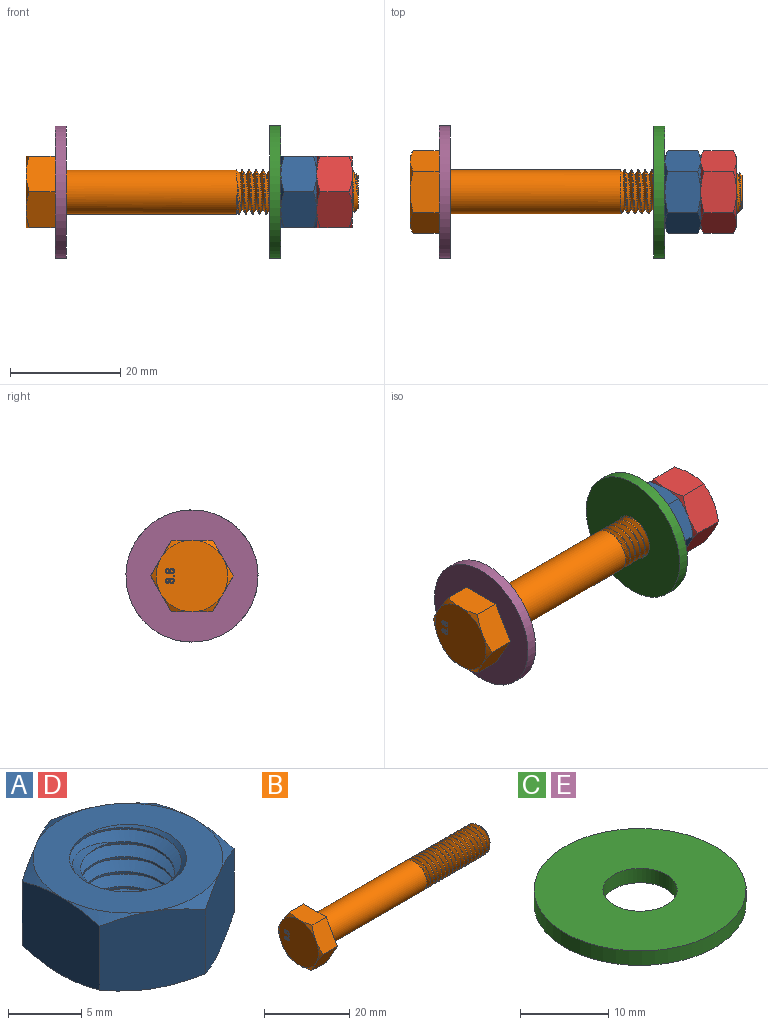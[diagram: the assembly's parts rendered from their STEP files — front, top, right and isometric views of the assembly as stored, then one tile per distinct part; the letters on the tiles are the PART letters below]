
ASSEMBLY  parts=5 mates=4
PART A: 27 faces, bbox 15.6x15.6x9.2 mm
  f0: cylinder r=4mm len=8mm, axis (0,0,-1), area 20.5mm2, adj f10,f11,f12,f13,f14
  f1: cylinder r=3.19mm len=6.38mm, axis (0,0,1), area 12.2mm2, adj f2,f3,f13,f14
  f2: cone r=4mm half-angle=45deg, axis (0,0,-1), area 13.3mm2, adj f1,f11,f13,f14
  f3: cone r=4mm half-angle=45deg, axis (0,0,1), area 13.2mm2, adj f1,f10,f12,f13,f14
  f4: plane 7.12x7.12mm, normal (-0.5,0.87,0), area 45.8mm2, adj f5,f9,f18,f19,f22,f23
  f5: plane 8.12x7.12mm, normal (-1,0,0), area 45.8mm2, adj f4,f6,f17,f18,f23,f24
  f6: plane 7.12x7.12mm, normal (-0.5,-0.87,0), area 45.8mm2, adj f5,f7,f16,f17,f24,f25
  f7: plane 7.12x7.12mm, normal (0.5,-0.87,0), area 45.8mm2, adj f6,f8,f15,f16,f25,f26
  f8: plane 8.12x7.12mm, normal (1,0,0), area 45.8mm2, adj f7,f9,f15,f20,f21,f26
  f9: plane 7.12x7.12mm, normal (0.5,0.87,0), area 45.8mm2, adj f4,f8,f19,f20,f21,f22
  f10: plane 13x13mm, normal (0,0,1), area 82.5mm2, adj f0,f3,f15,f16,f17,f18,f19,f20
  f11: plane 13x13mm, normal (0,0,-1), area 82.5mm2, adj f0,f2,f21,f22,f23,f24,f25,f26
  f12: plane 0.09x0.06mm, normal (-1,0,0), area 0mm2, adj f0,f3,f13
  f13: bspline ~8x7.98mm, area 96.9mm2, adj f0,f1,f2,f3,f12
  f14: bspline ~8.22x8mm, area 107.5mm2, adj f0,f1,f2,f3
  f15: cone r=6.5mm half-angle=60deg, axis (0,0,-1), area 4.2mm2, adj f7,f8,f10
  f16: cone r=6.5mm half-angle=60deg, axis (0,0,-1), area 4.2mm2, adj f6,f7,f10
  f17: cone r=6.5mm half-angle=60deg, axis (0,0,-1), area 4.2mm2, adj f5,f6,f10
  f18: cone r=6.5mm half-angle=60deg, axis (0,0,-1), area 4.2mm2, adj f4,f5,f10
  f19: cone r=6.5mm half-angle=60deg, axis (0,0,-1), area 4.2mm2, adj f4,f9,f10
  f20: cone r=6.5mm half-angle=60deg, axis (0,0,-1), area 4.2mm2, adj f8,f9,f10
  f21: cone r=6.5mm half-angle=60deg, axis (0,0,1), area 4.2mm2, adj f8,f9,f11
  f22: cone r=6.5mm half-angle=60deg, axis (0,0,1), area 4.2mm2, adj f4,f9,f11
  f23: cone r=6.5mm half-angle=60deg, axis (0,0,1), area 4.2mm2, adj f4,f5,f11
  f24: cone r=6.5mm half-angle=60deg, axis (0,0,1), area 4.2mm2, adj f5,f6,f11
  f25: cone r=6.5mm half-angle=60deg, axis (0,0,1), area 4.2mm2, adj f6,f7,f11
  f26: cone r=6.5mm half-angle=60deg, axis (0,0,1), area 4.2mm2, adj f7,f8,f11
PART B: 82 faces, bbox 61.2x15.6x15.6 mm
  f0: cone r=1000mm half-angle=45deg, axis (-1,0,0), area 13.5mm2, adj f19,f20,f21,f22,f23
  f1: cone r=3.06mm half-angle=45deg, axis (-1,0,0), area 16.1mm2, adj f2,f20,f21,f23,f32
  f2: cylinder r=4mm len=8mm, axis (1,0,0), area 2.2mm2, adj f1,f3,f21,f23
  f3: cylinder r=4mm len=8mm, axis (1,0,0), area 3.9mm2, adj f2,f4,f21,f23
  f4: cylinder r=4mm len=8mm, axis (1,0,0), area 3.9mm2, adj f3,f5,f21,f23
  f5: cylinder r=4mm len=8mm, axis (1,0,0), area 3.9mm2, adj f4,f6,f21,f23
  f6: cylinder r=4mm len=8mm, axis (1,0,0), area 3.9mm2, adj f5,f7,f21,f23
  f7: cylinder r=4mm len=8mm, axis (1,0,0), area 3.9mm2, adj f6,f8,f21,f23
  f8: cylinder r=4mm len=8mm, axis (1,0,0), area 3.9mm2, adj f7,f9,f21,f23
  f9: cylinder r=4mm len=8mm, axis (1,0,0), area 3.9mm2, adj f8,f10,f21,f23
  f10: cylinder r=4mm len=8mm, axis (1,0,0), area 3.9mm2, adj f9,f11,f21,f23
  f11: cylinder r=4mm len=8mm, axis (1,0,0), area 3.9mm2, adj f10,f12,f21,f23
  f12: cylinder r=4mm len=8mm, axis (1,0,0), area 3.9mm2, adj f11,f13,f21,f23
  f13: cylinder r=4mm len=8mm, axis (1,0,0), area 3.9mm2, adj f12,f14,f21,f23
  f14: cylinder r=4mm len=8mm, axis (1,0,0), area 3.9mm2, adj f13,f15,f21,f23
  f15: cylinder r=4mm len=8mm, axis (1,0,0), area 3.9mm2, adj f14,f16,f21,f23
  f16: cylinder r=4mm len=8mm, axis (1,0,0), area 3.9mm2, adj f15,f17,f21,f23
  f17: cylinder r=4mm len=8mm, axis (1,0,0), area 3.9mm2, adj f16,f18,f21,f23
  f18: cylinder r=4mm len=8mm, axis (1,0,0), area 3.9mm2, adj f17,f19,f21,f22,f23
  f19: cylinder r=4mm len=33.44mm, axis (1,0,0), area 830.5mm2, adj f0,f18,f22,f23,f24
  f20: cylinder r=3.19mm len=21.06mm, axis (1,0,0), area 66mm2, adj f0,f1,f21,f23
  f21: bspline ~23x7.99mm, area 371.9mm2, adj f0,f1,f2,f3,f4,f5,f6,f7
  f22: bspline ~8x7.99mm, area 3.7mm2, adj f0,f18,f19
  f23: bspline ~22.81x8mm, area 358.7mm2, adj f0,f1,f2,f3,f4,f5,f6,f7
  f24: plane 15.01x13mm, normal (1,0,0), area 96.1mm2, adj f19,f26,f27,f28,f29,f30,f31
  f25: plane 13x13mm, normal (-1,0,0), area 130.3mm2, adj f33,f34,f35,f36,f37,f38,f39,f40
  f26: plane 8.12x5.92mm, normal (0,0,-1), area 38.3mm2, adj f24,f27,f31,f35,f36
  f27: plane 7.12x5.92mm, normal (0,-0.87,-0.5), area 38.3mm2, adj f24,f26,f28,f34,f35
  f28: plane 7.12x5.92mm, normal (0,-0.87,0.5), area 38.3mm2, adj f24,f27,f29,f33,f34
  f29: plane 8.12x5.92mm, normal (0,0,1), area 38.3mm2, adj f24,f28,f30,f33,f38
  f30: plane 7.12x5.92mm, normal (0,0.87,0.5), area 38.3mm2, adj f24,f29,f31,f37,f38
  f31: plane 7.12x5.92mm, normal (0,0.87,-0.5), area 38.3mm2, adj f24,f26,f30,f36,f37
  f32: plane 6.13x6.13mm, normal (1,0,0), area 29.5mm2, adj f1
  f33: cone r=6.5mm half-angle=60deg, axis (1,0,0), area 4.2mm2, adj f25,f28,f29
  f34: cone r=6.5mm half-angle=60deg, axis (1,0,0), area 4.2mm2, adj f25,f27,f28
  f35: cone r=6.5mm half-angle=60deg, axis (1,0,0), area 4.2mm2, adj f25,f26,f27
  f36: cone r=6.5mm half-angle=60deg, axis (1,0,0), area 4.2mm2, adj f25,f26,f31
  f37: cone r=6.5mm half-angle=60deg, axis (1,0,0), area 4.2mm2, adj f25,f30,f31
  f38: cone r=6.5mm half-angle=60deg, axis (1,0,0), area 4.2mm2, adj f25,f29,f30
  f39: extruded ~0.39x0.29mm, area 0.1mm2, adj f25,f40,f46,f47
  f40: extruded ~0.31x0.25mm, area 0.1mm2, adj f25,f39,f41,f47
  f41: extruded ~0.43x0.39mm, area 0.2mm2, adj f25,f40,f42,f47
  f42: extruded ~0.44x0.39mm, area 0.2mm2, adj f25,f41,f43,f47
  f43: extruded ~0.3x0.25mm, area 0.1mm2, adj f25,f42,f44,f47
  f44: extruded ~0.4x0.29mm, area 0.1mm2, adj f25,f43,f45,f47
  f45: extruded ~0.49x0.47mm, area 0.2mm2, adj f25,f44,f46,f47
  f46: extruded ~0.49x0.47mm, area 0.2mm2, adj f25,f39,f45,f47
  f47: plane 1.56x0.99mm, normal (-1,0,0), area 0.8mm2, adj f39,f40,f41,f42,f43,f44,f45,f46
  f48: extruded ~0.25x0.24mm, area 0.1mm2, adj f47,f49,f51,f56
  f49: extruded ~0.25x0.24mm, area 0.1mm2, adj f47,f48,f50,f56
  f50: extruded ~0.25x0.24mm, area 0.1mm2, adj f47,f49,f51,f56
  f51: extruded ~0.25x0.24mm, area 0.1mm2, adj f47,f48,f50,f56
  f52: extruded ~0.29x0.29mm, area 0.1mm2, adj f47,f53,f55,f57
  f53: extruded ~0.3x0.3mm, area 0.1mm2, adj f47,f52,f54,f57
  f54: extruded ~0.3x0.29mm, area 0.1mm2, adj f47,f53,f55,f57
  f55: extruded ~0.3x0.3mm, area 0.1mm2, adj f47,f52,f54,f57
  f56: plane 0.47x0.43mm, normal (-1,0,0), area 0.2mm2, adj f48,f49,f50,f51
  f57: plane 0.59x0.59mm, normal (-1,0,0), area 0.3mm2, adj f52,f53,f54,f55
  f58: plane 0.25x0.2mm, normal (0,1,0), area 0mm2, adj f25,f59,f61,f62
  f59: plane 0.25x0.2mm, normal (0,0,1), area 0mm2, adj f25,f58,f60,f62
  f60: plane 0.25x0.2mm, normal (0,-1,0), area 0mm2, adj f25,f59,f61,f62
  f61: plane 0.25x0.2mm, normal (0,0,-1), area 0mm2, adj f25,f58,f60,f62
  f62: plane 0.2x0.2mm, normal (-1,0,0), area 0mm2, adj f58,f59,f60,f61
  f63: extruded ~0.39x0.29mm, area 0.1mm2, adj f25,f64,f70,f71
  f64: extruded ~0.31x0.25mm, area 0.1mm2, adj f25,f63,f65,f71
  f65: extruded ~0.43x0.39mm, area 0.2mm2, adj f25,f64,f66,f71
  f66: extruded ~0.44x0.39mm, area 0.2mm2, adj f25,f65,f67,f71
  f67: extruded ~0.3x0.25mm, area 0.1mm2, adj f25,f66,f68,f71
  f68: extruded ~0.4x0.29mm, area 0.1mm2, adj f25,f67,f69,f71
  f69: extruded ~0.49x0.47mm, area 0.2mm2, adj f25,f68,f70,f71
  f70: extruded ~0.49x0.47mm, area 0.2mm2, adj f25,f63,f69,f71
  f71: plane 1.56x0.99mm, normal (-1,0,0), area 0.8mm2, adj f63,f64,f65,f66,f67,f68,f69,f70
  f72: extruded ~0.25x0.24mm, area 0.1mm2, adj f71,f73,f75,f80
  f73: extruded ~0.25x0.24mm, area 0.1mm2, adj f71,f72,f74,f80
  f74: extruded ~0.25x0.24mm, area 0.1mm2, adj f71,f73,f75,f80
  f75: extruded ~0.25x0.24mm, area 0.1mm2, adj f71,f72,f74,f80
  f76: extruded ~0.29x0.29mm, area 0.1mm2, adj f71,f77,f79,f81
  f77: extruded ~0.3x0.3mm, area 0.1mm2, adj f71,f76,f78,f81
  f78: extruded ~0.3x0.29mm, area 0.1mm2, adj f71,f77,f79,f81
  f79: extruded ~0.3x0.3mm, area 0.1mm2, adj f71,f76,f78,f81
  f80: plane 0.47x0.43mm, normal (-1,0,0), area 0.2mm2, adj f72,f73,f74,f75
  f81: plane 0.59x0.59mm, normal (-1,0,0), area 0.3mm2, adj f76,f77,f78,f79
PART C: 4 faces, bbox 24x24x2 mm
  f0: cylinder r=4.2mm len=8.4mm, axis (0,0,-1), area 52.8mm2, adj f2,f3
  f1: cylinder r=12mm len=24mm, axis (0,0,-1), area 150.8mm2, adj f2,f3
  f2: plane 24x24mm, normal (0,0,1), area 397mm2, adj f0,f1
  f3: plane 24x24mm, normal (0,0,-1), area 397mm2, adj f0,f1
PART D: same geometry as A
PART E: same geometry as C
PLACE A rot(axis=(0.71,0,-0.71),180deg) t=(-68.27,-5.7,-280.06)mm
PLACE B t=(-87.67,-5.7,-280.06)mm
PLACE C rot(axis=(0.58,-0.58,-0.58),120deg) t=(-71.52,-38.13,-248.49)mm
PLACE D rot(axis=(0.71,0,-0.71),180deg) t=(-61.77,-5.7,-280.06)mm
PLACE E rot(axis=(0.71,0,-0.71),180deg) t=(-110.52,-37.27,-312.48)mm
MATE fastened E.f0 <-> B.f1  axis (-1,0,0) through (-112.52,-5.7,-280.06)mm
MATE fastened D.f0 <-> A.f0  axis (-1,0,0) through (-65.02,-5.7,-280.06)mm
MATE fastened A.f0 <-> C.f0  axis (-1,0,0) through (-71.52,-5.7,-280.06)mm
MATE fastened C.f0 <-> E.f0  axis (-1,0,0) through (-73.52,-5.7,-280.06)mm
